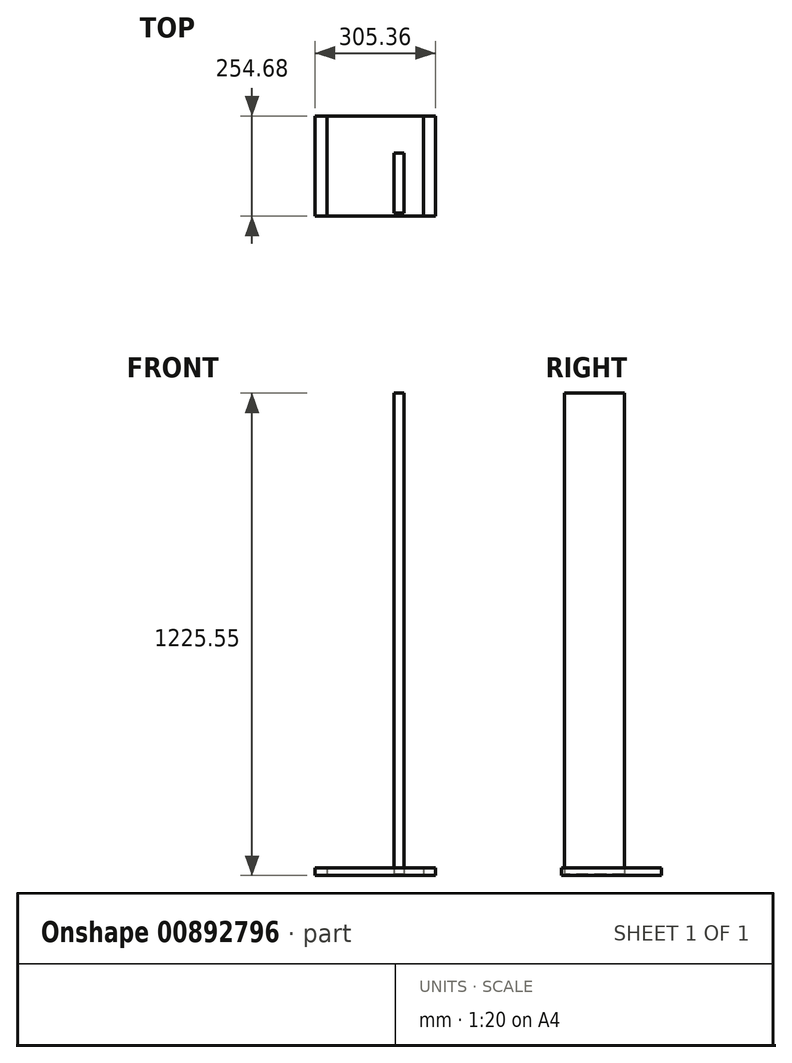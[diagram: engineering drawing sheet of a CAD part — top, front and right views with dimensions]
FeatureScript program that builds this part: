
annotation { "Feature Type Name" : "Feature", "Feature Type Description" : "" }
export const myFeature = defineFeature(function(context is Context, id is Id, definition is map)
    precondition{}
    {
        {
            var Q0;
            Q0=qCreatedBy(makeId("Top.planeOp"),FACE);
            var sketch = newSketch(context, id + "F0", { "sketchPlane" : qUnion([Q0])});
            skLineSegment(sketch, "E0.bottom", {"start": v(152.68, -127.34) * mm, "end": v(-152.68, -127.34) * mm});
            skLineSegment(sketch, "E0.top", {"start": v(152.68, 127.34) * mm, "end": v(-152.68, 127.34) * mm});
            skLineSegment(sketch, "E0.left", {"start": v(152.68, -127.34) * mm, "end": v(152.68, 127.34) * mm});
            skLineSegment(sketch, "E0.right", {"start": v(-152.68, -127.34) * mm, "end": v(-152.68, 127.34) * mm});
            skPoint(sketch, "E0.middle", {"position": v(0, 0) * mm});
            skSolve(sketch);
        }
        {
            var Q0;
            Q0=makeQuery(id+"F0.imprint","IMPRINT",FACE,{"disambiguationData":[TD([[makeQuery(id+"F0.imprint","IMPRINT",EDGE,{"derivedFrom":sQuery(id+"F0.wireOp",EDGE,"E0.bottom")}),-1.0]])]});
            extrude(context, id + "F1", {"entities" : qUnion([Q0]), "depth" : 19.05 * mm, "offsetDistance" : 25.4 * mm});
        }
        {
            var Q0;
            Q0=qCreatedBy(makeId("Top.planeOp"),FACE);
            var sketch = newSketch(context, id + "F2", { "sketchPlane" : qUnion([Q0])});
            skLineSegment(sketch, "E1.bottom", {"start": v(72.96, 32.98) * mm, "end": v(47.56, 32.98) * mm});
            skLineSegment(sketch, "E1.top", {"start": v(72.96, -119.42) * mm, "end": v(47.56, -119.42) * mm});
            skLineSegment(sketch, "E1.left", {"start": v(72.96, 32.98) * mm, "end": v(72.96, -119.42) * mm});
            skLineSegment(sketch, "E1.right", {"start": v(47.56, 32.98) * mm, "end": v(47.56, -119.42) * mm});
            skPoint(sketch, "E1.middle", {"position": v(60.26, -43.22) * mm});
            skSolve(sketch);
        }
        {
            var Q0;
            Q0=makeQuery(id+"F2.imprint","IMPRINT",FACE,{"disambiguationData":[TD([[makeQuery(id+"F2.imprint","IMPRINT",EDGE,{"derivedFrom":sQuery(id+"F2.wireOp",EDGE,"E1.bottom")}),1.0]])]});
            extrude(context, id + "F3", {"entities" : qUnion([Q0]), "depth" : 3.17 * mm, "offsetDistance" : 25.4 * mm});
        }
        {
            var Q0;
            Q0 = qSketchRegion(id + "F2", true);
            extrude(context, id + "F4", {"entities" : qUnion([Q0]), "depth" : 1225.55 * mm, "offsetDistance" : 25.4 * mm});
        }
        {
            var Q0;
            Q0=qCreatedBy(makeId("Top.planeOp"),FACE);
            var sketch = newSketch(context, id + "F5", { "sketchPlane" : qUnion([Q0])});
            skLineSegment(sketch, "E2.bottom", {"start": v(123.09, -126.7) * mm, "end": v(-123.09, -126.7) * mm});
            skLineSegment(sketch, "E2.top", {"start": v(123.09, 126.7) * mm, "end": v(-123.09, 126.7) * mm});
            skLineSegment(sketch, "E2.left", {"start": v(123.09, -126.7) * mm, "end": v(123.09, 126.7) * mm});
            skLineSegment(sketch, "E2.right", {"start": v(-123.09, -126.7) * mm, "end": v(-123.09, 126.7) * mm});
            skPoint(sketch, "E2.middle", {"position": v(0, 0) * mm});
            skSolve(sketch);
        }
        {
            var Q0;
            Q0 = qSketchRegion(id + "F5", true);
            extrude(context, id + "F6", {"entities" : qUnion([Q0]), "depth" : 19.05 * mm, "offsetDistance" : 25.4 * mm});
        }
    });
